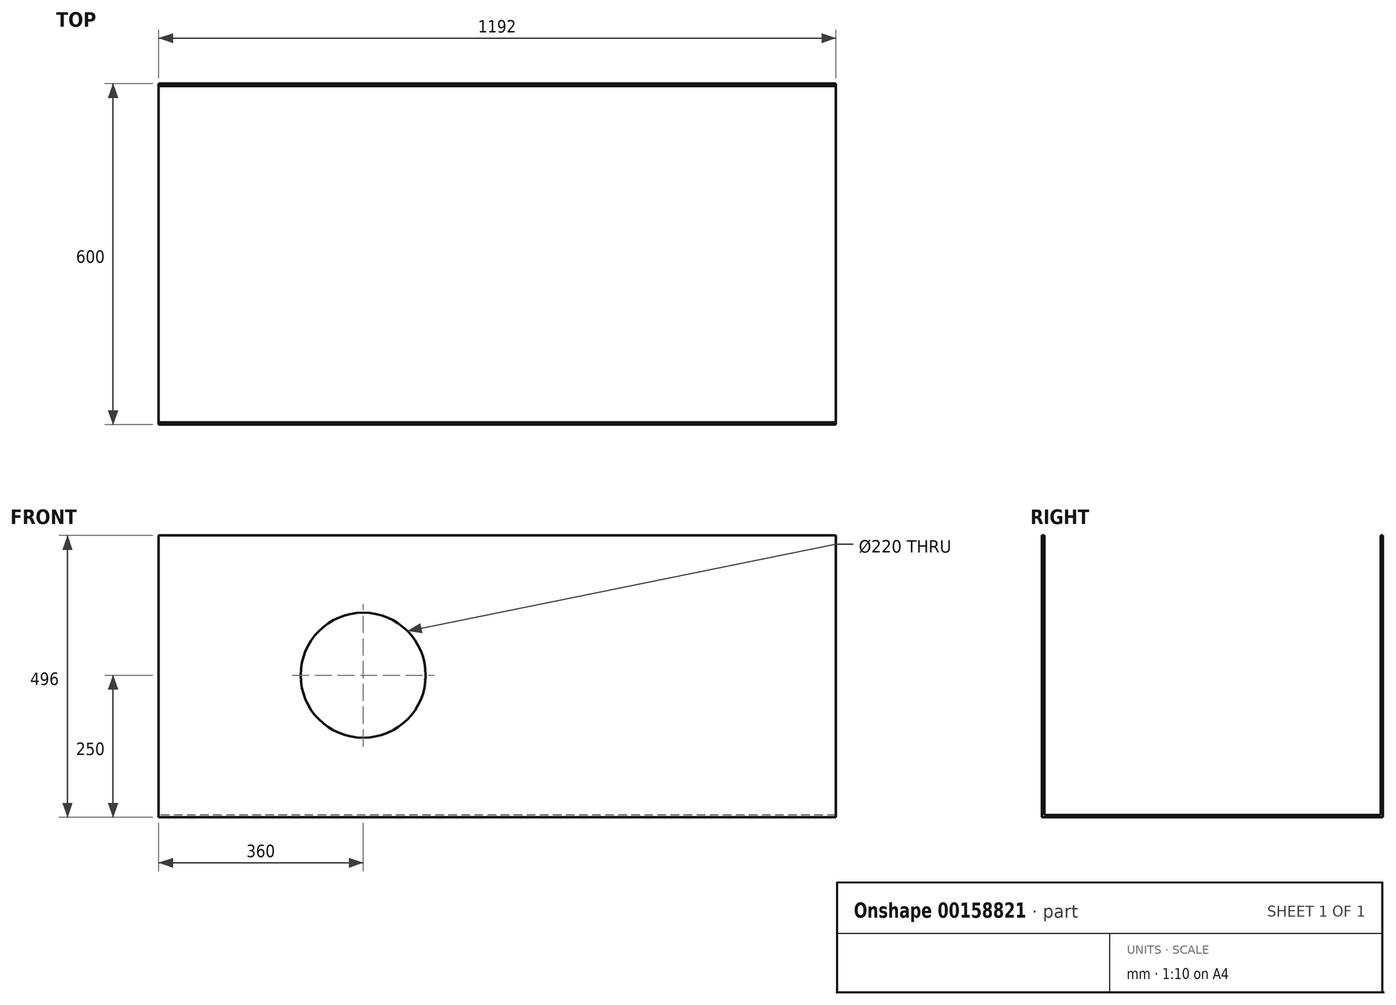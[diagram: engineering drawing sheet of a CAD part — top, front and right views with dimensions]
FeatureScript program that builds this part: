
annotation { "Feature Type Name" : "Feature", "Feature Type Description" : "" }
export const myFeature = defineFeature(function(context is Context, id is Id, definition is map)
    precondition{}
    {
        {
            var Q0;
            Q0=qCreatedBy(makeId("Front.planeOp"),FACE);
            var sketch = newSketch(context, id + "F0", { "sketchPlane" : qUnion([Q0])});
            skLineSegment(sketch, "E0.bottom", {"start": v(0, 0) * mm, "end": v(1192, 0) * mm});
            skLineSegment(sketch, "E0.top", {"start": v(0, 496) * mm, "end": v(1192, 496) * mm});
            skLineSegment(sketch, "E0.left", {"start": v(0, 0) * mm, "end": v(0, 496) * mm});
            skLineSegment(sketch, "E0.right", {"start": v(1192, 0) * mm, "end": v(1192, 496) * mm});
            skCircle(sketch, "E1", {"center": v(360, 250) * mm, "radius": 110 * mm});
            skSolve(sketch);
        }
        {
            var Q0;
            Q0 = qSketchRegion(id + "F0", true);
            extrude(context, id + "F1", {"entities" : qUnion([Q0]), "depth" : 4 * mm});
        }
        {
            var Q0;
            Q0=qCreatedBy(makeId("Right.planeOp"),FACE);
            var sketch = newSketch(context, id + "F2", { "sketchPlane" : qUnion([Q0])});
            skPoint(sketch, "E2.0", {"position": v(-2, 0) * mm});
            skPoint(sketch, "E3.0", {"position": v(-4, 4) * mm});
            skLineSegment(sketch, "E4.bottom", {"start": v(-4, 4) * mm, "end": v(596, 4) * mm});
            skLineSegment(sketch, "E4.top", {"start": v(-4, 0) * mm, "end": v(596, 0) * mm});
            skLineSegment(sketch, "E4.left", {"start": v(-4, 4) * mm, "end": v(-4, 0) * mm});
            skLineSegment(sketch, "E4.right", {"start": v(596, 4) * mm, "end": v(596, 0) * mm});
            skLineSegment(sketch, "E5.bottom", {"start": v(596, 0) * mm, "end": v(592, 0) * mm});
            skLineSegment(sketch, "E5.top", {"start": v(596, 496) * mm, "end": v(592, 496) * mm});
            skLineSegment(sketch, "E5.left", {"start": v(596, 0) * mm, "end": v(596, 496) * mm});
            skLineSegment(sketch, "E5.right", {"start": v(592, 0) * mm, "end": v(592, 496) * mm});
            skSolve(sketch);
        }
        {
            var Q0;
            Q0 = qSketchRegion(id + "F2", true);
            extrude(context, id + "F3", {"entities" : qUnion([Q0]), "operationType" : NewBodyOperationType.ADD, "depth" : 1192 * mm});
        }
    });
